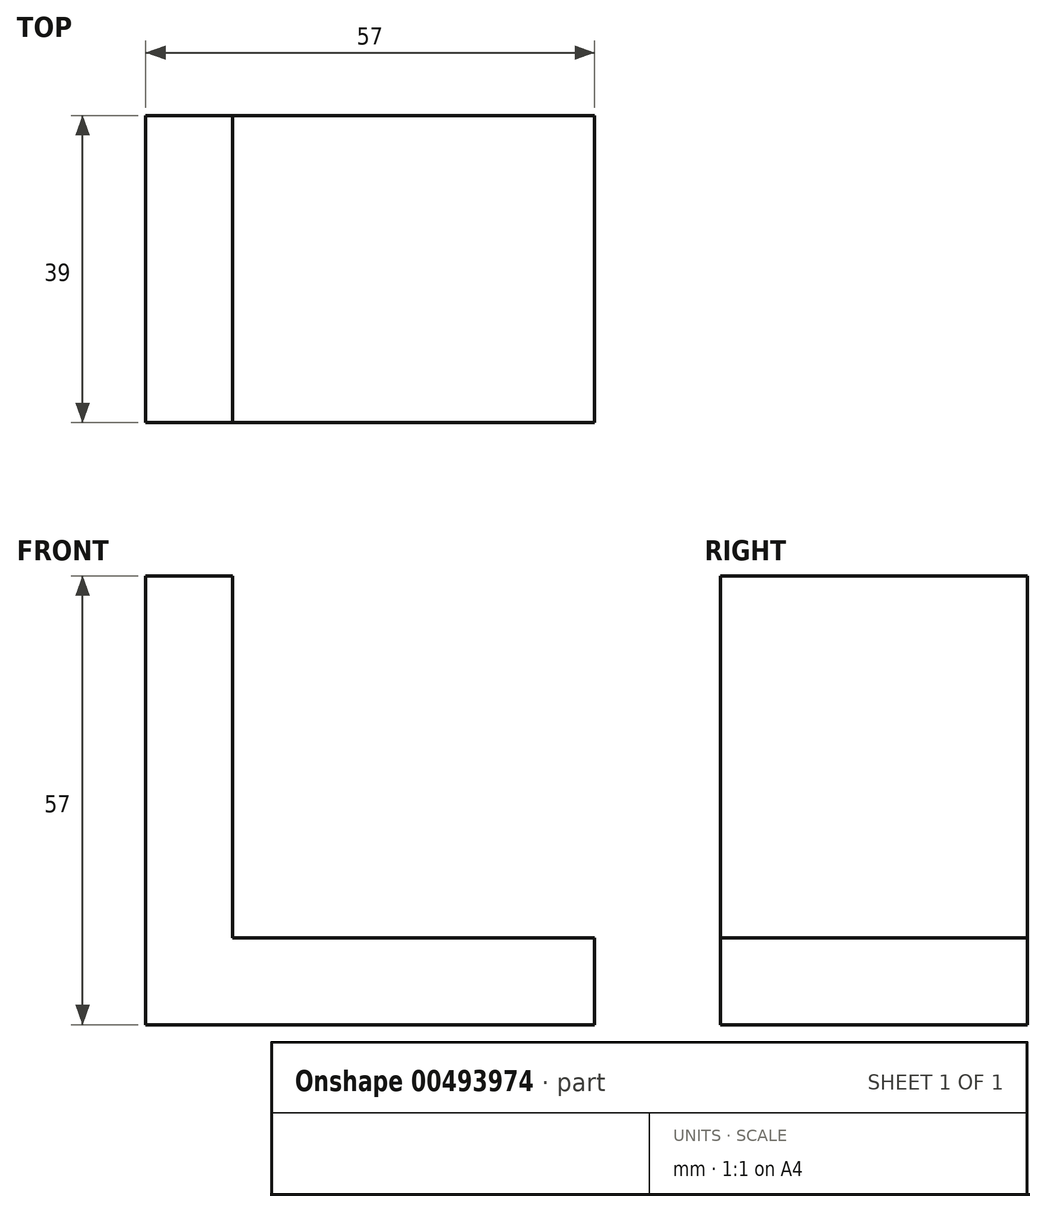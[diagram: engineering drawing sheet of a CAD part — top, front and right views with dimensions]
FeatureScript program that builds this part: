
annotation { "Feature Type Name" : "Feature", "Feature Type Description" : "" }
export const myFeature = defineFeature(function(context is Context, id is Id, definition is map)
    precondition{}
    {
        {
            var Q0;
            Q0=qCreatedBy(makeId("Front.planeOp"),FACE);
            var sketch = newSketch(context, id + "F0", { "sketchPlane" : qUnion([Q0])});
            skLineSegment(sketch, "E0.bottom", {"start": v(0, 0) * mm, "end": v(11, 0) * mm});
            skLineSegment(sketch, "E0.top", {"start": v(0, 57) * mm, "end": v(11, 57) * mm});
            skLineSegment(sketch, "E0.left", {"start": v(0, 0) * mm, "end": v(0, 57) * mm});
            skLineSegment(sketch, "E0.right", {"start": v(11, 11) * mm, "end": v(11, 57) * mm});
            skLineSegment(sketch, "E1.bottom", {"start": v(0, 0) * mm, "end": v(57, 0) * mm});
            skLineSegment(sketch, "E1.top", {"start": v(11, 11) * mm, "end": v(57, 11) * mm});
            skLineSegment(sketch, "E1.left", {"start": v(0, 0) * mm, "end": v(0, 11) * mm});
            skLineSegment(sketch, "E1.right", {"start": v(57, 0) * mm, "end": v(57, 11) * mm});
            skSolve(sketch);
        }
        {
            var Q0;
            Q0=makeQuery(id+"F0.imprint","IMPRINT",FACE,{"disambiguationData":[TD([[makeQuery(id+"F0.imprint","IMPRINT",EDGE,{"derivedFrom":sQuery(id+"F0.wireOp",EDGE,"E0.top")}),-1.0]])]});
            extrude(context, id + "F1", {"entities" : qUnion([Q0]), "depth" : 39 * mm});
        }
    });
